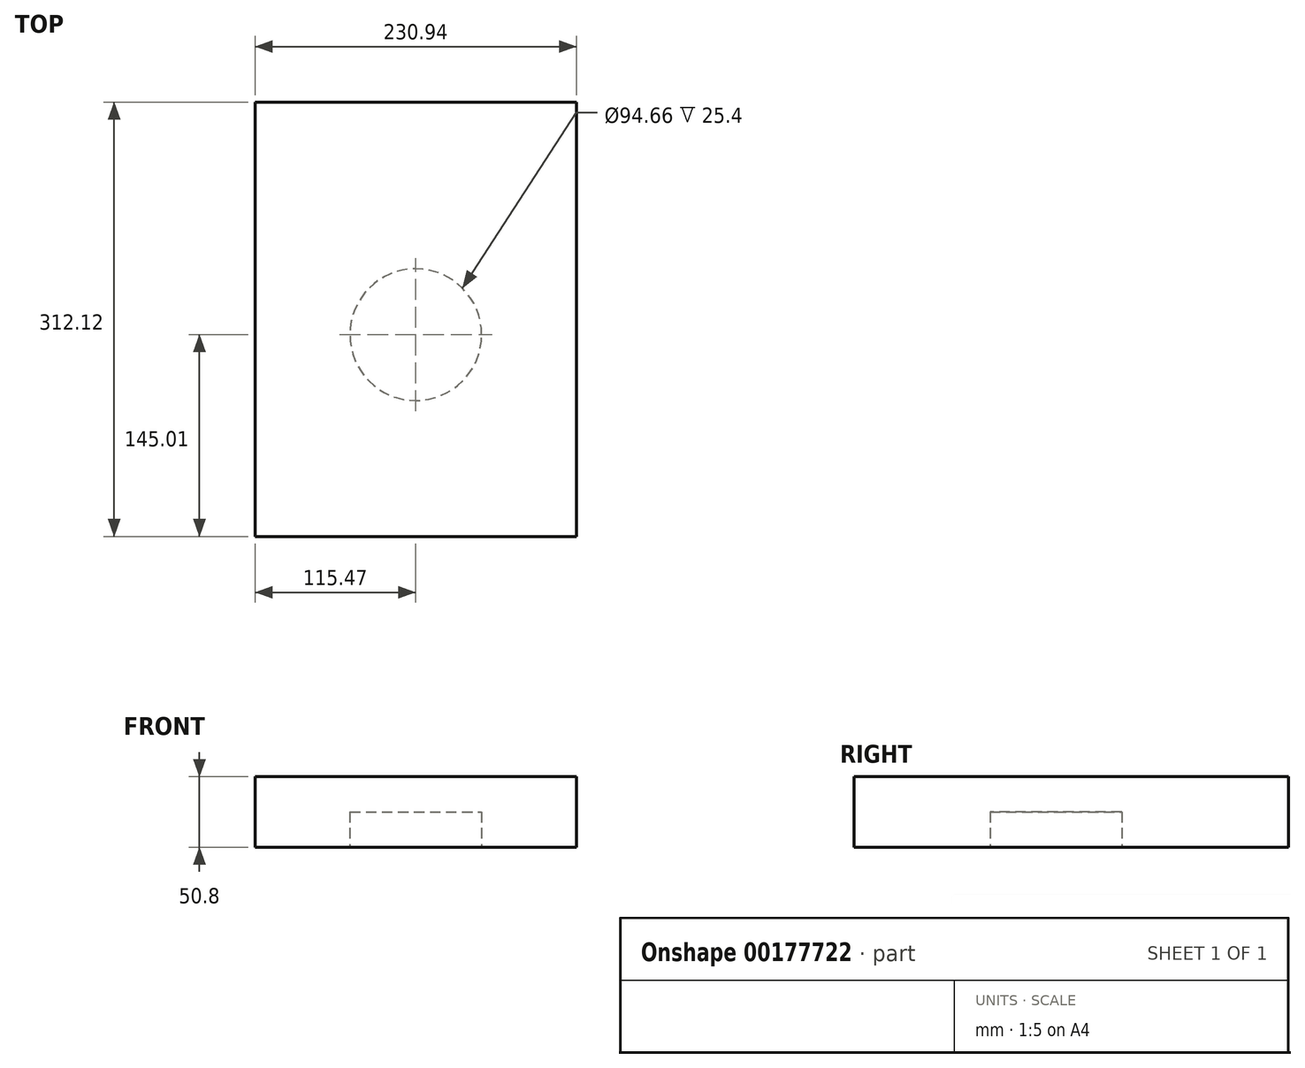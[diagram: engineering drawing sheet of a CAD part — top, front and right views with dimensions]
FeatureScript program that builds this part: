
annotation { "Feature Type Name" : "Feature", "Feature Type Description" : "" }
export const myFeature = defineFeature(function(context is Context, id is Id, definition is map)
    precondition{}
    {
        {
            var Q0;
            Q0=qCreatedBy(makeId("Top.planeOp"),FACE);
            var sketch = newSketch(context, id + "F0", { "sketchPlane" : qUnion([Q0])});
            skLineSegment(sketch, "E0.bottom", {"start": v(115.47, -145) * mm, "end": v(-115.47, -145) * mm});
            skLineSegment(sketch, "E0.top", {"start": v(115.47, 167.1) * mm, "end": v(-115.47, 167.1) * mm});
            skLineSegment(sketch, "E0.left", {"start": v(115.47, -145) * mm, "end": v(115.47, 167.1) * mm});
            skLineSegment(sketch, "E0.right", {"start": v(-115.47, -145) * mm, "end": v(-115.47, 167.1) * mm});
            skPoint(sketch, "E0.middle", {"position": v(0, 11.05) * mm});
            skSolve(sketch);
        }
        {
            var Q0;
            Q0=makeQuery(id+"F0.imprint","IMPRINT",FACE,{"disambiguationData":[TD([[makeQuery(id+"F0.imprint","IMPRINT",EDGE,{"derivedFrom":sQuery(id+"F0.wireOp",EDGE,"E0.bottom")}),-1.0]])]});
            extrude(context, id + "F1", {"entities" : qUnion([Q0]), "depth" : 50.8 * mm});
        }
        {
            var Q0;
            Q0=makeQuery(id+"F1.opExtrude","CAP_FACE",FACE,{"disambiguationData":[OSD([sQuery(id+"F0.wireOp",EDGE,"E0.bottom"),sQuery(id+"F0.wireOp",EDGE,"E0.top"),sQuery(id+"F0.wireOp",EDGE,"E0.left"),sQuery(id+"F0.wireOp",EDGE,"E0.right")])],"isStart":true});
            var sketch = newSketch(context, id + "F2", { "sketchPlane" : qUnion([Q0])});
            skCircle(sketch, "E1", {"center": v(0, 0) * mm, "radius": 47.33 * mm});
            skSolve(sketch);
        }
        {
            var Q0;
            Q0 = qSketchRegion(id + "F2", true);
            extrude(context, id + "F3", {"entities" : qUnion([Q0]), "operationType" : NewBodyOperationType.REMOVE, "oppositeDirection" : true, "depth" : 25.4 * mm});
        }
    });
